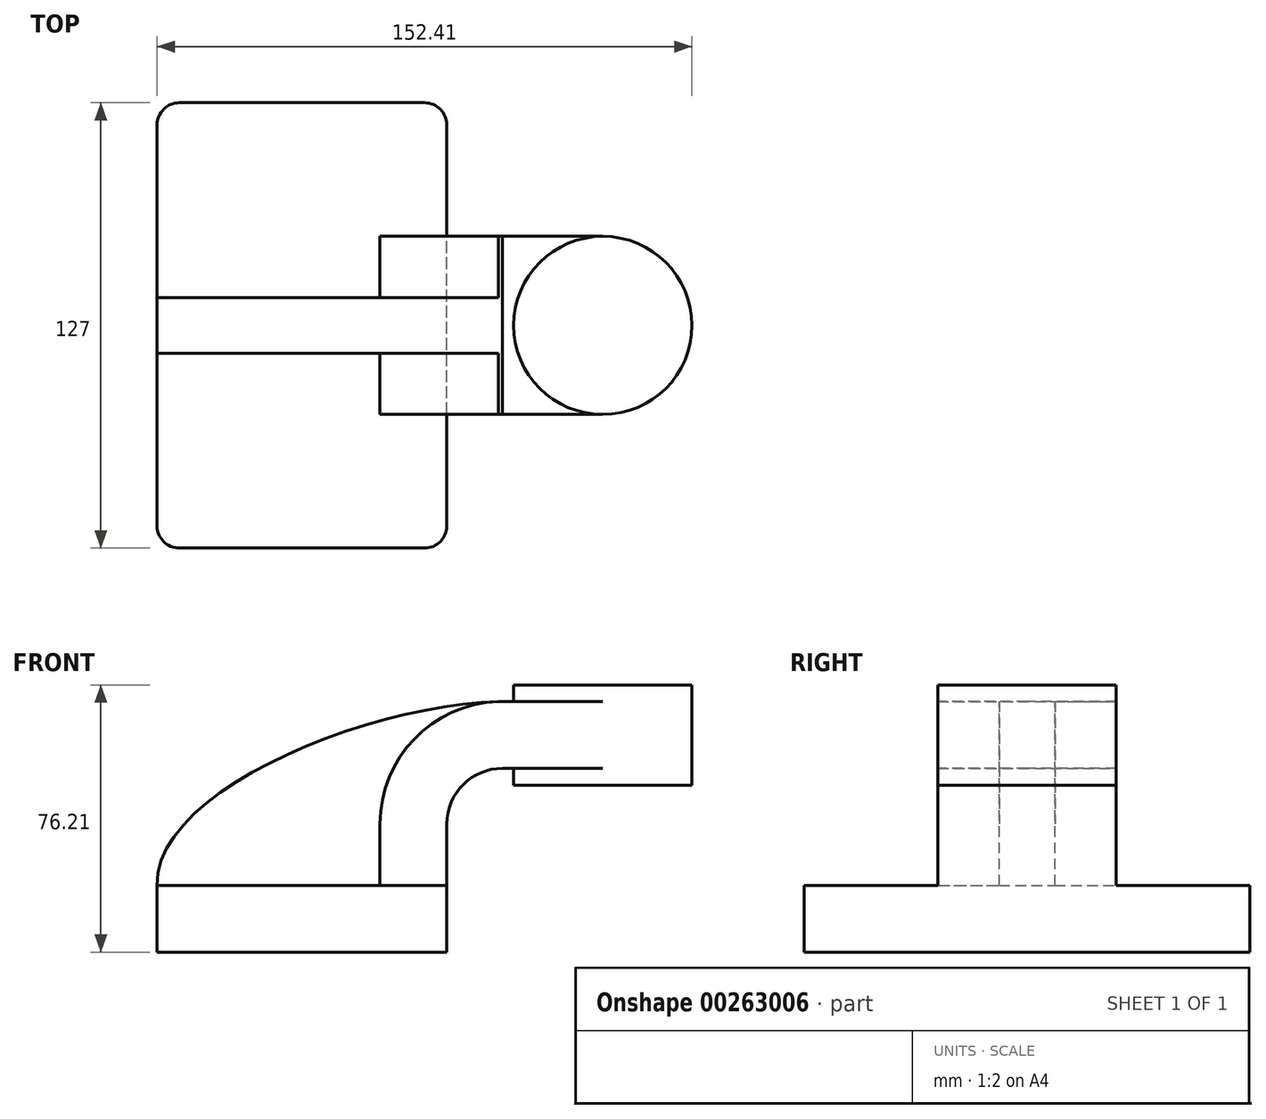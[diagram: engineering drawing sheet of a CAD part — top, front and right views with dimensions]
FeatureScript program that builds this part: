
annotation { "Feature Type Name" : "Feature", "Feature Type Description" : "" }
export const myFeature = defineFeature(function(context is Context, id is Id, definition is map)
    precondition{}
    {
        {
            var Q0;
            Q0=qCreatedBy(makeId("Front.planeOp"),FACE);
            var sketch = newSketch(context, id + "F0", { "sketchPlane" : qUnion([Q0])});
            skLineSegment(sketch, "E0.bottom", {"start": v(-41.28, 9.52) * mm, "end": v(41.28, 9.53) * mm});
            skLineSegment(sketch, "E0.top", {"start": v(-41.27, -9.53) * mm, "end": v(41.28, -9.53) * mm});
            skLineSegment(sketch, "E0.left", {"start": v(-41.28, 9.52) * mm, "end": v(-41.28, -9.53) * mm});
            skLineSegment(sketch, "E0.right", {"start": v(41.28, 9.53) * mm, "end": v(41.28, -9.52) * mm});
            skPoint(sketch, "E0.middle", {"position": v(0, 0) * mm});
            skLineSegment(sketch, "E1.bottom", {"start": v(60.32, 66.68) * mm, "end": v(111.12, 66.68) * mm});
            skLineSegment(sketch, "E1.top", {"start": v(60.32, 38.1) * mm, "end": v(111.12, 38.1) * mm});
            skLineSegment(sketch, "E1.left", {"start": v(60.32, 66.67) * mm, "end": v(60.32, 38.1) * mm});
            skLineSegment(sketch, "E1.right", {"start": v(111.12, 66.67) * mm, "end": v(111.12, 38.1) * mm});
            skPoint(sketch, "E1.middle", {"position": v(85.72, 52.39) * mm});
            skLineSegment(sketch, "E2", {"start": v(41.27, 9.53) * mm, "end": v(41.27, 27) * mm});
            skArc(sketch, "E3", {"start": v(41.27, 27) * mm, "mid": v(45.92, 38.23) * mm, "end": v(57.15, 42.88) * mm});
            skLineSegment(sketch, "E4", {"start": v(57.15, 42.88) * mm, "end": v(85.72, 42.88) * mm});
            skLineSegment(sketch, "E5.0", {"start": v(57.15, 61.93) * mm, "end": v(85.72, 61.93) * mm});
            skArc(sketch, "E5.1", {"start": v(22.22, 27) * mm, "mid": v(32.45, 51.7) * mm, "end": v(57.15, 61.93) * mm});
            skLineSegment(sketch, "E5.2", {"start": v(22.22, 9.53) * mm, "end": v(22.22, 27) * mm});
            skLineSegment(sketch, "E6", {"start": v(85.72, 42.88) * mm, "end": v(85.72, 66.68) * mm});
            skFitSpline(sketch, "E7", {"points": [v(-41.28, 9.53) * mm, v(57.15, 61.93) * mm], "startDerivative": vector(-2.2, 82.47) * mm, "endDerivative": vector(110.31, 1.12) * mm});
            skLineSegment(sketch, "E8", {"start": v(85.72, 42.88) * mm, "end": v(85.72, 38.1) * mm});
            skSolve(sketch);
        }
        {
            var Q0;
            Q0=makeQuery(id+"F0.imprint","IMPRINT",FACE,{"disambiguationData":[TD([[makeQuery(id+"F0.imprint","IMPRINT",EDGE,{"derivedFrom":sQuery(id+"F0.wireOp",EDGE,"E0.top")}),1.0]])]});
            extrude(context, id + "F1", {"entities" : qUnion([Q0]), "endBound" : BoundingType.SYMMETRIC, "depth" : 127 * mm});
        }
        {
            var Q0;
            {var subQ6=sQuery(id+"F0.wireOp",EDGE,"E2");Q0=makeQuery(id+"F0.imprint","IMPRINT",FACE,{"disambiguationData":[TD([[makeQuery(id+"F0.imprint","IMPRINT",EDGE,{"derivedFrom":subQ6}),1.0]])]});}
            var Q1;
            {var subQ0=sQuery(id+"F0.wireOp",EDGE,"E5.0");var subQ1=sQuery(id+"F0.wireOp",EDGE,"E1.left");var subQ2=makeQuery(id+"F0.imprint","INTERSECT",VERTEX,{"derivedFrom":[subQ1,subQ0]});Q1=makeQuery(id+"F0.imprint","IMPRINT",FACE,{"disambiguationData":[TD([[makeQuery(id+"F0.imprint","IMPRINT",EDGE,{"disambiguationData":[TD([[subQ2,-1.0]])],"derivedFrom":subQ1}),1.0]])]});}
            extrude(context, id + "F2", {"entities" : qUnion([Q0, Q1]), "operationType" : NewBodyOperationType.ADD, "endBound" : BoundingType.SYMMETRIC, "depth" : 50.8 * mm});
        }
        {
            var Q0;
            {var subQ3=sQuery(id+"F0.wireOp",EDGE,"E5.2");Q0=makeQuery(id+"F0.imprint","IMPRINT",FACE,{"disambiguationData":[TD([[makeQuery(id+"F0.imprint","IMPRINT",EDGE,{"derivedFrom":subQ3}),1.0]])]});}
            extrude(context, id + "F3", {"entities" : qUnion([Q0]), "operationType" : NewBodyOperationType.ADD, "endBound" : BoundingType.SYMMETRIC, "depth" : 15.88 * mm});
        }
        {
            var Q0;
            {var subQ0=sQuery(id+"F0.wireOp",EDGE,"E1.right");Q0=makeQuery(id+"F0.imprint","IMPRINT",FACE,{"disambiguationData":[TD([[makeQuery(id+"F0.imprint","IMPRINT",EDGE,{"derivedFrom":subQ0}),-1.0]])]});}
            var Q1;
            Q1=sQuery(id+"F0.wireOp",EDGE,"E6");
            revolve(context, id + "F4", {"operationType" : NewBodyOperationType.ADD, "entities" : qUnion([Q0]), "axis" : qUnion([Q1]), "revolveType" : RevolveType.FULL});
        }
        {
            var Q0;
            Q0=makeQuery(id+"F1.opExtrude","CAP_EDGE",EDGE,{"disambiguationData":[OSD([sQuery(id+"F0.wireOp",EDGE,"E0.left")])],"isStart":true});
            var Q1;
            Q1=makeQuery(id+"F1.opExtrude","CAP_EDGE",EDGE,{"disambiguationData":[OSD([sQuery(id+"F0.wireOp",EDGE,"E0.left")])],"isStart":false});
            var Q2;
            Q2=makeQuery(id+"F1.opExtrude","CAP_EDGE",EDGE,{"disambiguationData":[OSD([sQuery(id+"F0.wireOp",EDGE,"E0.right")])],"isStart":false});
            var Q3;
            Q3=makeQuery(id+"F1.opExtrude","CAP_EDGE",EDGE,{"disambiguationData":[OSD([sQuery(id+"F0.wireOp",EDGE,"E0.right")])],"isStart":true});
            fillet(context, id + "F5", {"entities" : qUnion([Q0, Q1, Q2, Q3]), "radius" : 6.35 * mm, "tangentPropagation" : true, "allowEdgeOverflow" : false});
        }
    });
